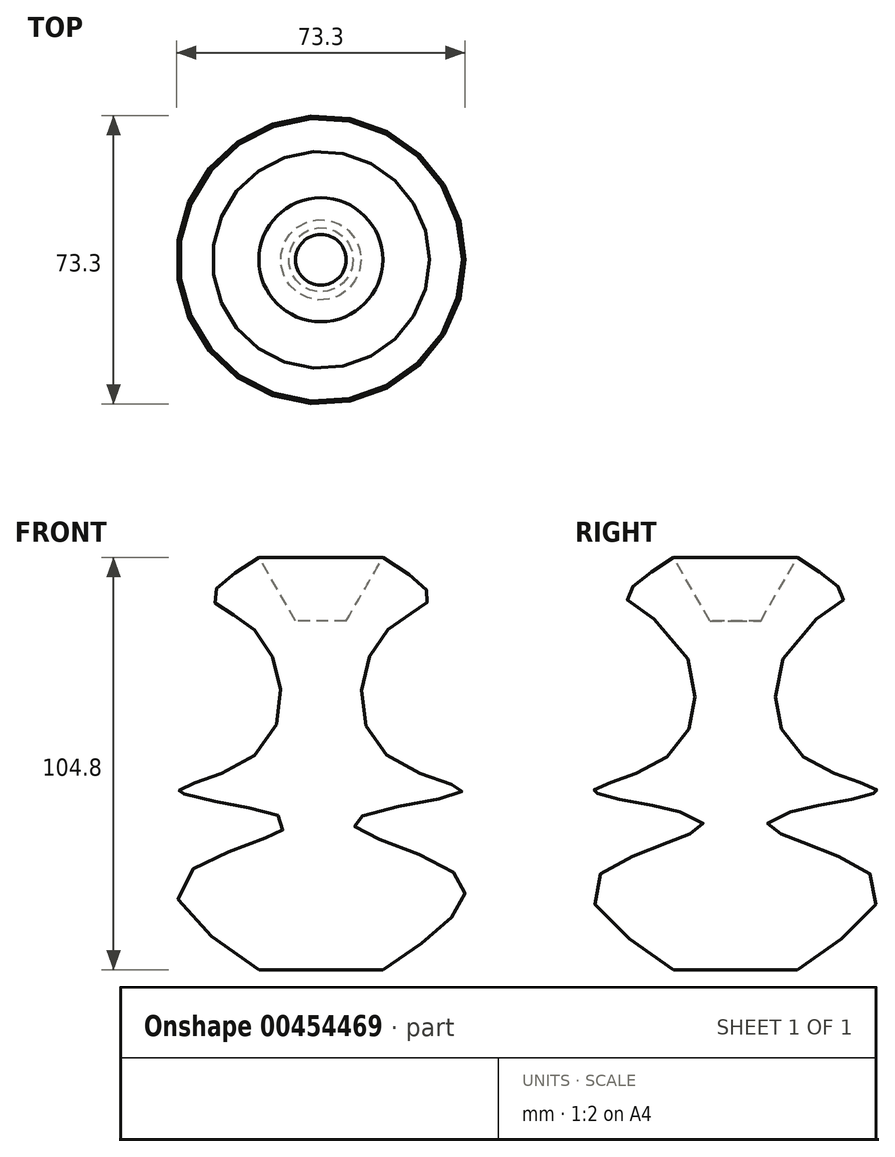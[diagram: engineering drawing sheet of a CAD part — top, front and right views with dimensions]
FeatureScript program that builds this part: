
annotation { "Feature Type Name" : "Feature", "Feature Type Description" : "" }
export const myFeature = defineFeature(function(context is Context, id is Id, definition is map)
    precondition{}
    {
        {
            var Q0;
            Q0=qCreatedBy(makeId("Front.planeOp"),FACE);
            var sketch = newSketch(context, id + "F0", { "sketchPlane" : qUnion([Q0])});
            skLineSegment(sketch, "E0", {"start": v(0, 43.46) * mm, "end": v(0, -45.25) * mm});
            skLineSegment(sketch, "E1", {"start": v(0, -45.25) * mm, "end": v(15.74, -45.25) * mm});
            skLineSegment(sketch, "E2", {"start": v(0.36, 43.46) * mm, "end": v(6.44, 43.46) * mm});
            skLineSegment(sketch, "E3", {"start": v(6.44, 43.46) * mm, "end": v(15.74, 59.55) * mm});
            skFitSpline(sketch, "E4", {"points": [v(15.74, -45.25) * mm, v(35.41, -22) * mm, v(8.23, -7.7) * mm, v(35.77, 0) * mm, v(15.74, 10.2) * mm, v(15.74, 39.88) * mm, v(27.54, 49.18) * mm, v(15.74, 59.55) * mm], "startDerivative": vector(233.4, 157.51) * mm, "endDerivative": vector(-160.06, 100.32) * mm});
            skLineSegment(sketch, "E5", {"start": v(0.36, 43.46) * mm, "end": v(0, 43.46) * mm});
            skPoint(sketch, "E6.orphan", {"position": v(0, 59.55) * mm});
            skSolve(sketch);
        }
        {
            var Q0;
            Q0=makeQuery(id+"F0.imprint","IMPRINT",FACE,{"disambiguationData":[TD([[makeQuery(id+"F0.imprint","IMPRINT",EDGE,{"derivedFrom":sQuery(id+"F0.wireOp",EDGE,"E0")}),1.0]])]});
            var Q1;
            Q1=sQuery(id+"F0.wireOp",EDGE,"E0");
            revolve(context, id + "F1", {"entities" : qUnion([Q0]), "axis" : qUnion([Q1]), "revolveType" : RevolveType.FULL});
        }
    });
